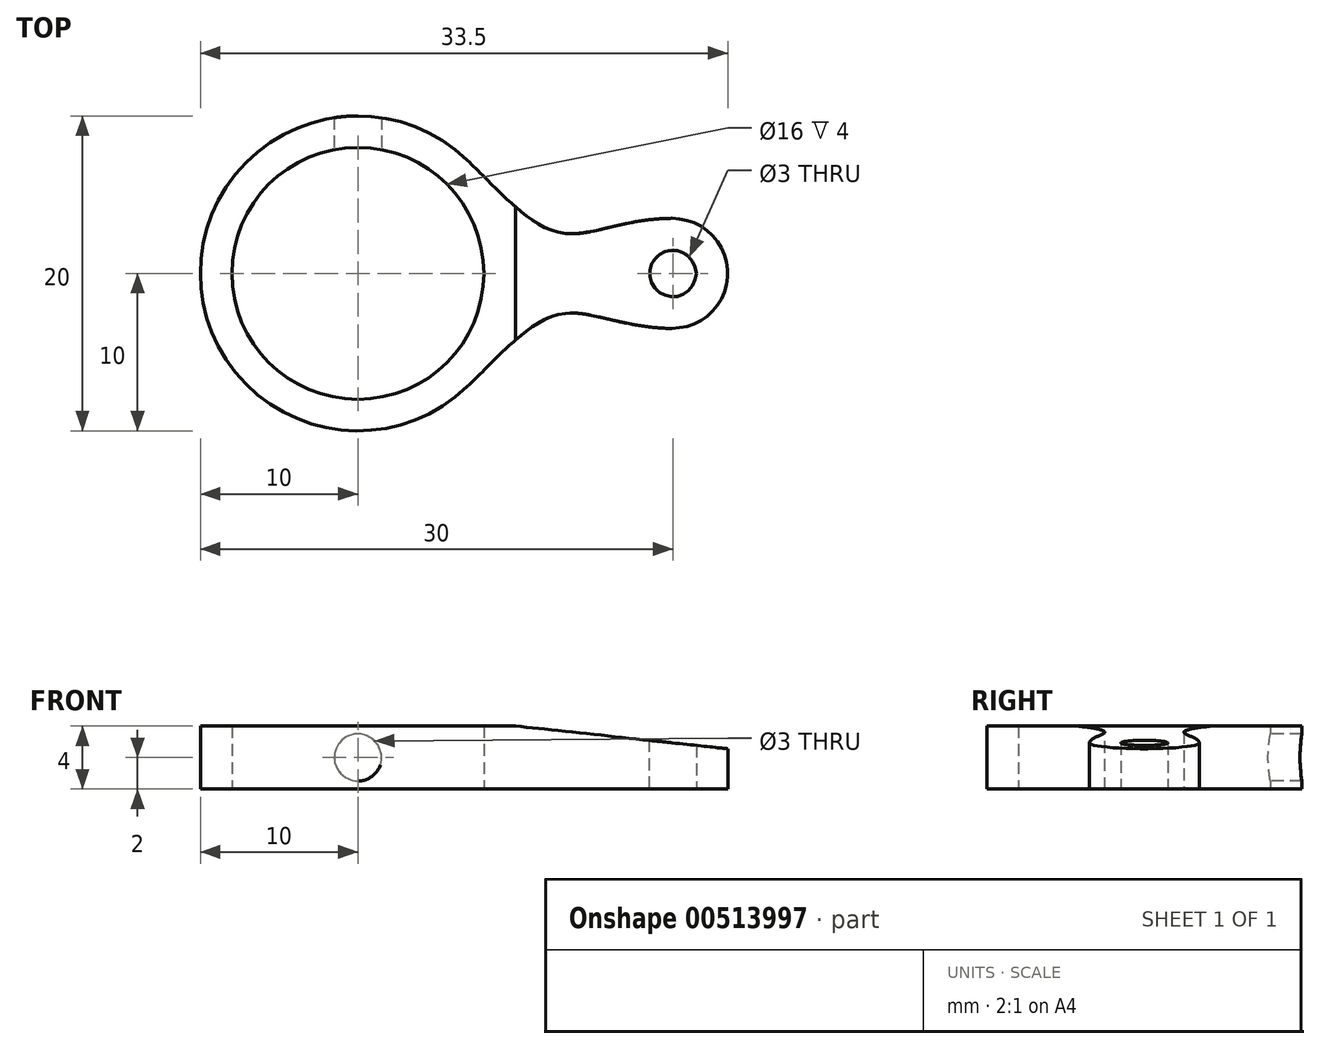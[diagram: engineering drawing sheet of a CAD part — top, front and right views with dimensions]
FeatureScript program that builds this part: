
annotation { "Feature Type Name" : "Feature", "Feature Type Description" : "" }
export const myFeature = defineFeature(function(context is Context, id is Id, definition is map)
    precondition{}
    {
        {
            var Q0;
            Q0=qCreatedBy(makeId("Top.planeOp"),FACE);
            var sketch = newSketch(context, id + "F0", { "sketchPlane" : qUnion([Q0])});
            skCircle(sketch, "E0", {"center": v(0, 0) * mm, "radius": 8 * mm});
            skCircle(sketch, "E1", {"center": v(0, 0) * mm, "radius": 10 * mm});
            skFitSpline(sketch, "E2", {"points": [v(6.95, 7.2) * mm, v(12.73, 2.6) * mm, v(19.94, 3.5) * mm], "startDerivative": vector(12.22, -11.8) * mm, "endDerivative": vector(20.58, 0.33) * mm});
            skCircle(sketch, "E3", {"center": v(20, 0) * mm, "radius": 3.5 * mm});
            skCircle(sketch, "E4", {"center": v(20, 0) * mm, "radius": 1.5 * mm});
            skFitSpline(sketch, "E5.MirrorCS", {"points": [v(6.95, -7.2) * mm, v(12.73, -2.6) * mm, v(19.94, -3.5) * mm], "startDerivative": vector(12.22, 11.8) * mm, "endDerivative": vector(20.58, -0.33) * mm});
            skSolve(sketch);
        }
        {
            var Q0;
            Q0=makeQuery(id+"F0.imprint","IMPRINT",FACE,{"disambiguationData":[TD([[makeQuery(id+"F0.imprint","IMPRINT",EDGE,{"derivedFrom":sQuery(id+"F0.wireOp",EDGE,"E0")}),-1.0]])]});
            var Q1;
            {var subQ0=sQuery(id+"F0.wireOp",EDGE,"E2");Q1=makeQuery(id+"F0.imprint","IMPRINT",FACE,{"disambiguationData":[TD([[makeQuery(id+"F0.imprint","IMPRINT",EDGE,{"derivedFrom":subQ0}),-1.0]])]});}
            var Q2;
            Q2=makeQuery(id+"F0.imprint","IMPRINT",FACE,{"disambiguationData":[TD([[makeQuery(id+"F0.imprint","IMPRINT",EDGE,{"derivedFrom":sQuery(id+"F0.wireOp",EDGE,"E4")}),-1.0]])]});
            extrude(context, id + "F1", {"entities" : qUnion([Q0, Q1, Q2]), "depth" : 4 * mm});
        }
        {
            var Q0;
            Q0=qCreatedBy(makeId("Front.planeOp"),FACE);
            var sketch = newSketch(context, id + "F2", { "sketchPlane" : qUnion([Q0])});
            skCircle(sketch, "E6", {"center": v(0, 2) * mm, "radius": 1.5 * mm});
            skSolve(sketch);
        }
        {
            var Q0;
            Q0=makeQuery(id+"F2.imprint","IMPRINT",FACE,{"disambiguationData":[TD([[makeQuery(id+"F2.imprint","IMPRINT",EDGE,{"derivedFrom":sQuery(id+"F2.wireOp",EDGE,"E6")}),1.0]])]});
            extrude(context, id + "F3", {"entities" : qUnion([Q0]), "operationType" : NewBodyOperationType.REMOVE, "oppositeDirection" : true, "depth" : 25 * mm});
        }
        {
            var Q0;
            Q0=qCreatedBy(makeId("Front.planeOp"),FACE);
            var sketch = newSketch(context, id + "F4", { "sketchPlane" : qUnion([Q0])});
            skLineSegment(sketch, "E7", {"start": v(-10, 4) * mm, "end": v(10, 4) * mm});
            skLineSegment(sketch, "E8", {"start": v(10, 4) * mm, "end": v(24, 2.5) * mm});
            skLineSegment(sketch, "E9", {"start": v(24, 2.5) * mm, "end": v(24, -2.68) * mm});
            skLineSegment(sketch, "E10", {"start": v(24, -2.68) * mm, "end": v(-10, -3.14) * mm});
            skLineSegment(sketch, "E11", {"start": v(-10, -3.14) * mm, "end": v(-10, 4) * mm});
            skSolve(sketch);
        }
        {
            var Q0;
            Q0=makeQuery(id+"F4.imprint","IMPRINT",FACE,{"disambiguationData":[TD([[makeQuery(id+"F4.imprint","IMPRINT",EDGE,{"derivedFrom":sQuery(id+"F4.wireOp",EDGE,"E7")}),-1.0]])]});
            extrude(context, id + "F5", {"entities" : qUnion([Q0]), "operationType" : NewBodyOperationType.INTERSECT, "depth" : 25 * mm, "symmetric" : true});
        }
    });
